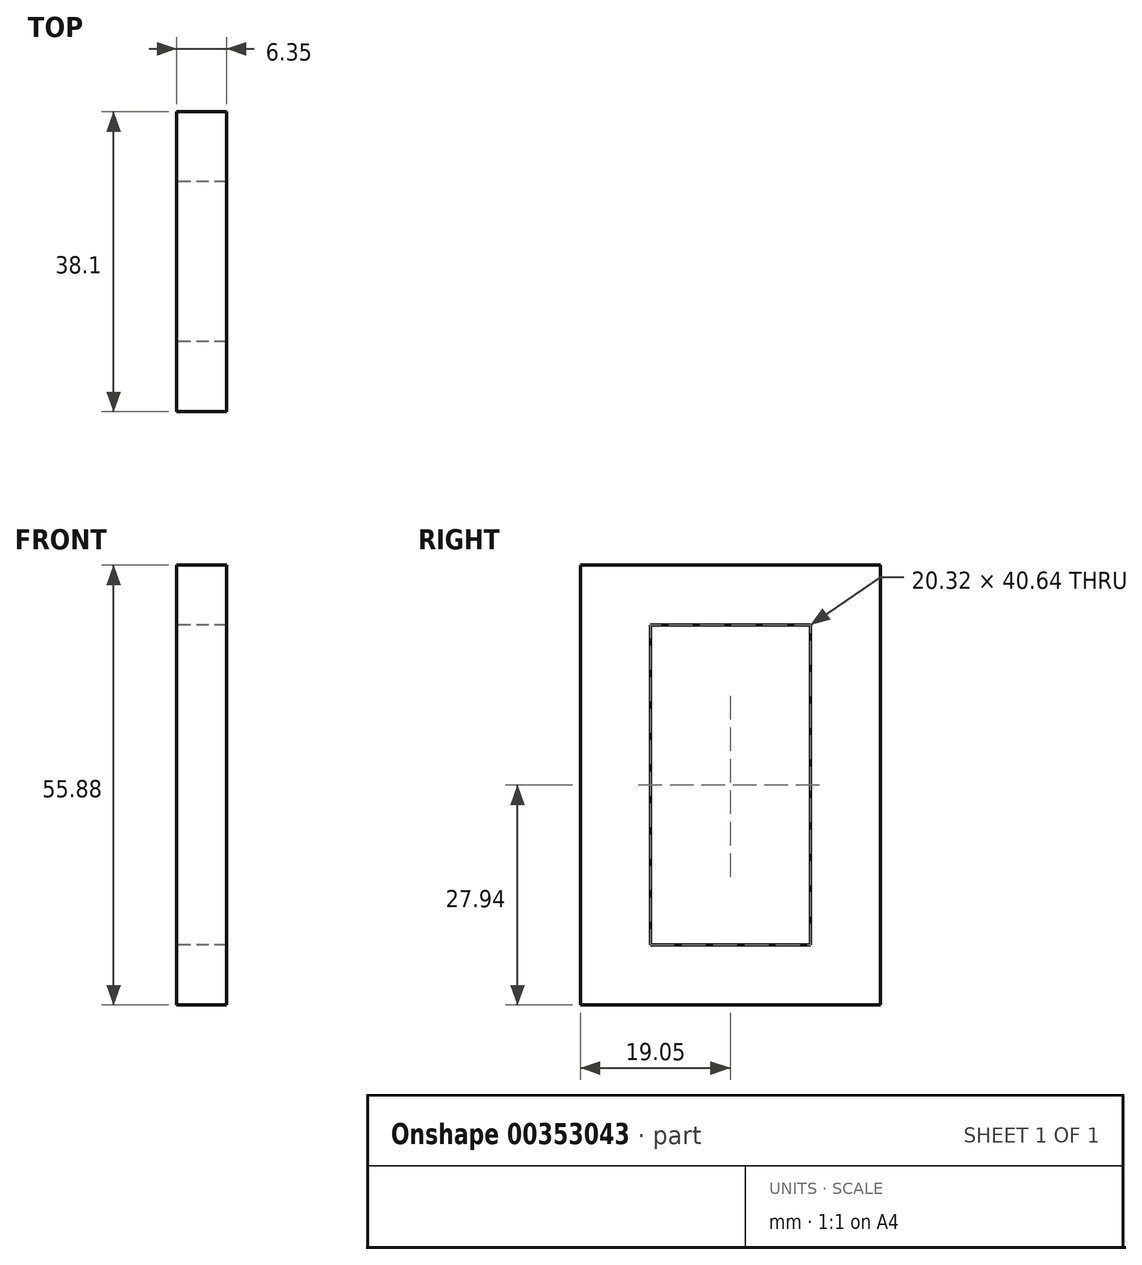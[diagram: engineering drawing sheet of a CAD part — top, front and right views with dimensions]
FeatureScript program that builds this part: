
annotation { "Feature Type Name" : "Feature", "Feature Type Description" : "" }
export const myFeature = defineFeature(function(context is Context, id is Id, definition is map)
    precondition{}
    {
        {
            var Q0;
            Q0=qCreatedBy(makeId("Right.planeOp"),FACE);
            var sketch = newSketch(context, id + "F0", { "sketchPlane" : qUnion([Q0])});
            skLineSegment(sketch, "E0.bottom", {"start": v(0, 0) * mm, "end": v(38.1, 0) * mm});
            skLineSegment(sketch, "E0.top", {"start": v(0, 55.88) * mm, "end": v(38.1, 55.88) * mm});
            skLineSegment(sketch, "E0.left", {"start": v(0, 0) * mm, "end": v(0, 55.88) * mm});
            skLineSegment(sketch, "E0.right", {"start": v(38.1, 0) * mm, "end": v(38.1, 55.88) * mm});
            skLineSegment(sketch, "E1", {"start": v(0, 27.94) * mm, "end": v(38.1, 27.94) * mm});
            skLineSegment(sketch, "E2", {"start": v(19.05, 55.88) * mm, "end": v(19.05, 0) * mm});
            skLineSegment(sketch, "E3.bottom", {"start": v(29.21, 7.62) * mm, "end": v(8.89, 7.62) * mm});
            skLineSegment(sketch, "E3.top", {"start": v(29.21, 48.26) * mm, "end": v(8.9, 48.26) * mm});
            skLineSegment(sketch, "E3.left", {"start": v(29.21, 7.62) * mm, "end": v(29.21, 48.26) * mm});
            skLineSegment(sketch, "E3.right", {"start": v(8.89, 7.62) * mm, "end": v(8.9, 48.26) * mm});
            skPoint(sketch, "E3.middle", {"position": v(19.05, 27.94) * mm});
            skSolve(sketch);
        }
        {
            var Q0;
            {var subQ1=sQuery(id+"F0.wireOp",EDGE,"E0.left");var subQ5=sQuery(id+"F0.wireOp",EDGE,"E0.bottom");var subQ6=makeQuery(id+"F0.imprint","INTERSECT",VERTEX,{"derivedFrom":[subQ5,subQ1]});Q0=makeQuery(id+"F0.imprint","IMPRINT",FACE,{"disambiguationData":[TD([[makeQuery(id+"F0.imprint","IMPRINT",EDGE,{"disambiguationData":[TD([[subQ6,-1.0]])],"derivedFrom":subQ5}),1.0]])]});}
            var Q1;
            {var subQ1=sQuery(id+"F0.wireOp",EDGE,"E0.bottom");var subQ6=sQuery(id+"F0.wireOp",EDGE,"E0.right");var subQ10=makeQuery(id+"F0.imprint","INTERSECT",VERTEX,{"derivedFrom":[subQ1,subQ6]});Q1=makeQuery(id+"F0.imprint","IMPRINT",FACE,{"disambiguationData":[TD([[makeQuery(id+"F0.imprint","IMPRINT",EDGE,{"disambiguationData":[TD([[subQ10,1.0]])],"derivedFrom":subQ1}),1.0]])]});}
            var Q2;
            {var subQ1=sQuery(id+"F0.wireOp",EDGE,"E0.right");var subQ6=sQuery(id+"F0.wireOp",EDGE,"E0.top");var subQ10=makeQuery(id+"F0.imprint","INTERSECT",VERTEX,{"derivedFrom":[subQ6,subQ1]});Q2=makeQuery(id+"F0.imprint","IMPRINT",FACE,{"disambiguationData":[TD([[makeQuery(id+"F0.imprint","IMPRINT",EDGE,{"disambiguationData":[TD([[subQ10,1.0]])],"derivedFrom":subQ6}),-1.0]])]});}
            var Q3;
            {var subQ1=sQuery(id+"F0.wireOp",EDGE,"E0.left");var subQ9=sQuery(id+"F0.wireOp",EDGE,"E0.top");var subQ10=makeQuery(id+"F0.imprint","INTERSECT",VERTEX,{"derivedFrom":[subQ9,subQ1]});Q3=makeQuery(id+"F0.imprint","IMPRINT",FACE,{"disambiguationData":[TD([[makeQuery(id+"F0.imprint","IMPRINT",EDGE,{"disambiguationData":[TD([[subQ10,-1.0]])],"derivedFrom":subQ9}),-1.0]])]});}
            extrude(context, id + "F1", {"entities" : qUnion([Q0, Q1, Q2, Q3]), "depth" : 6.35 * mm, "offsetDistance" : 25.4 * mm});
        }
    });
